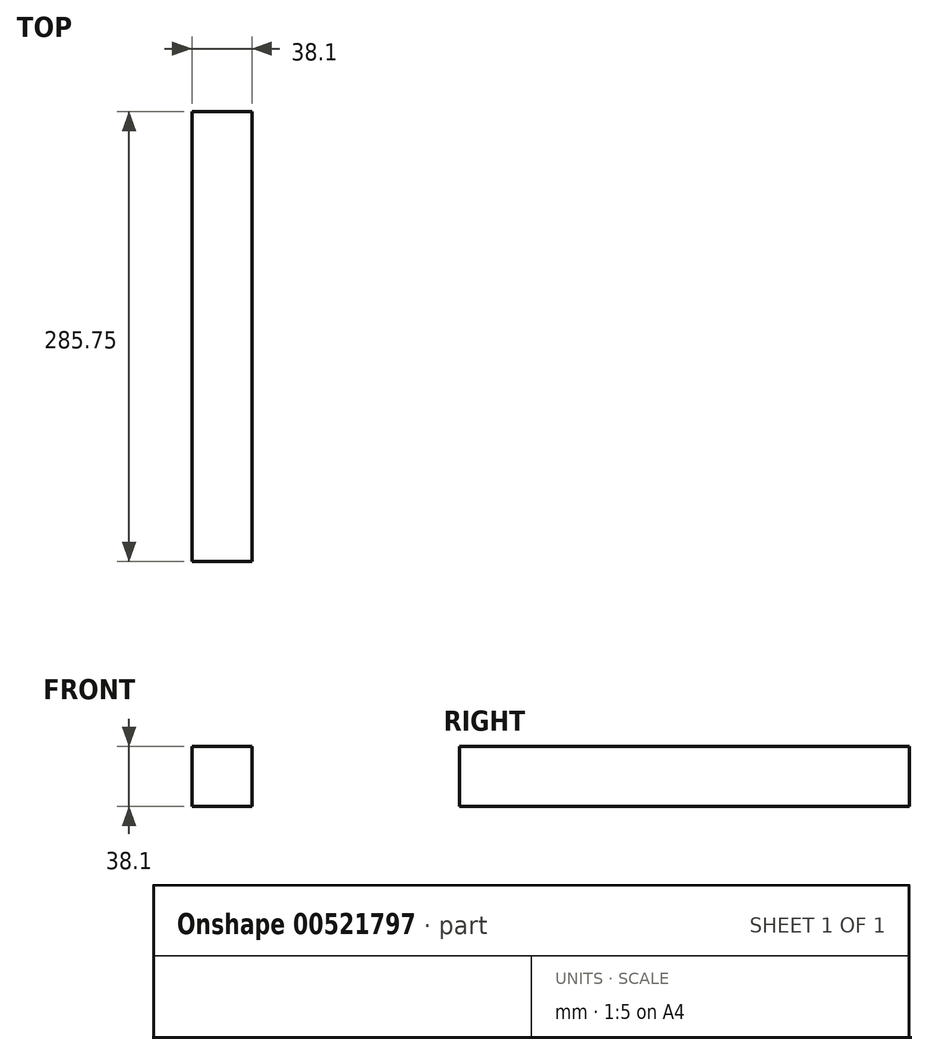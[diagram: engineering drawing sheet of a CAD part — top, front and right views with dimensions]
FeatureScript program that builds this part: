
annotation { "Feature Type Name" : "Feature", "Feature Type Description" : "" }
export const myFeature = defineFeature(function(context is Context, id is Id, definition is map)
    precondition{}
    {
        {
            var Q0;
            Q0=qCreatedBy(makeId("Front.planeOp"),FACE);
            var sketch = newSketch(context, id + "F0", { "sketchPlane" : qUnion([Q0])});
            skLineSegment(sketch, "E0.bottom", {"start": v(0, 0) * mm, "end": v(38.1, 0) * mm});
            skLineSegment(sketch, "E0.top", {"start": v(0, 38.1) * mm, "end": v(38.1, 38.1) * mm});
            skLineSegment(sketch, "E0.left", {"start": v(0, 0) * mm, "end": v(0, 38.1) * mm});
            skLineSegment(sketch, "E0.right", {"start": v(38.1, 0) * mm, "end": v(38.1, 38.1) * mm});
            skSolve(sketch);
        }
        {
            var Q0;
            Q0=qSketchRegion(id+"F0",true);
            extrude(context, id + "F1", {"entities" : qUnion([Q0]), "oppositeDirection" : true, "depth" : 285.75 * mm, "offsetDistance" : 25.4 * mm});
        }
    });
